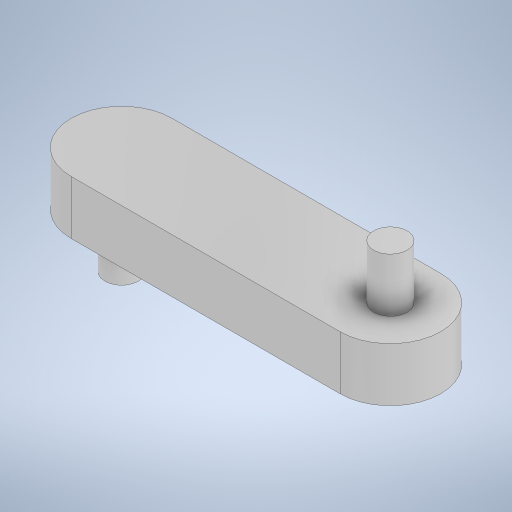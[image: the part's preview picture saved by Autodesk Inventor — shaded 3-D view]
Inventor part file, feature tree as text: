
AUTODESK INVENTOR PART (.ipt)
format: ipt  version: 2024 (Build 280153000, 153)  size: 244,224 bytes
history: native  units: in
note: dims shown in document units (in); Inventor stores cm internally (conversion verified against a paired STEP export)
features: extrude x3, sketch x3
ambient origin geometry x8: Origin, YZ Plane, XZ Plane, XY Plane, X Axis, Y Axis, Z Axis, Center Point
bodies: Solid1 (feature_tree)
feature tree (6):
  extrude  "Extrusion1"  Depth=0.75in
  extrude  "Extrusion4"  Depth=2.0in
  extrude  "Extrusion5"  Depth=0.75in
  sketch  "Sketch1"  dims[d1=2.0in d4=0.75in]
  sketch  "Sketch4"  dims[d6=0.4in d7=0.0in d14=2.0in]
  sketch  "Sketch5"  dims[d15=2.0in d16=0.75in d17=0.25in d18=0.4in d19=0.0in d20=0.25in d21=0.4in d22=0.0in d8=0.5in d9=0.0344in d10=0.5in d11=0.0344in]
